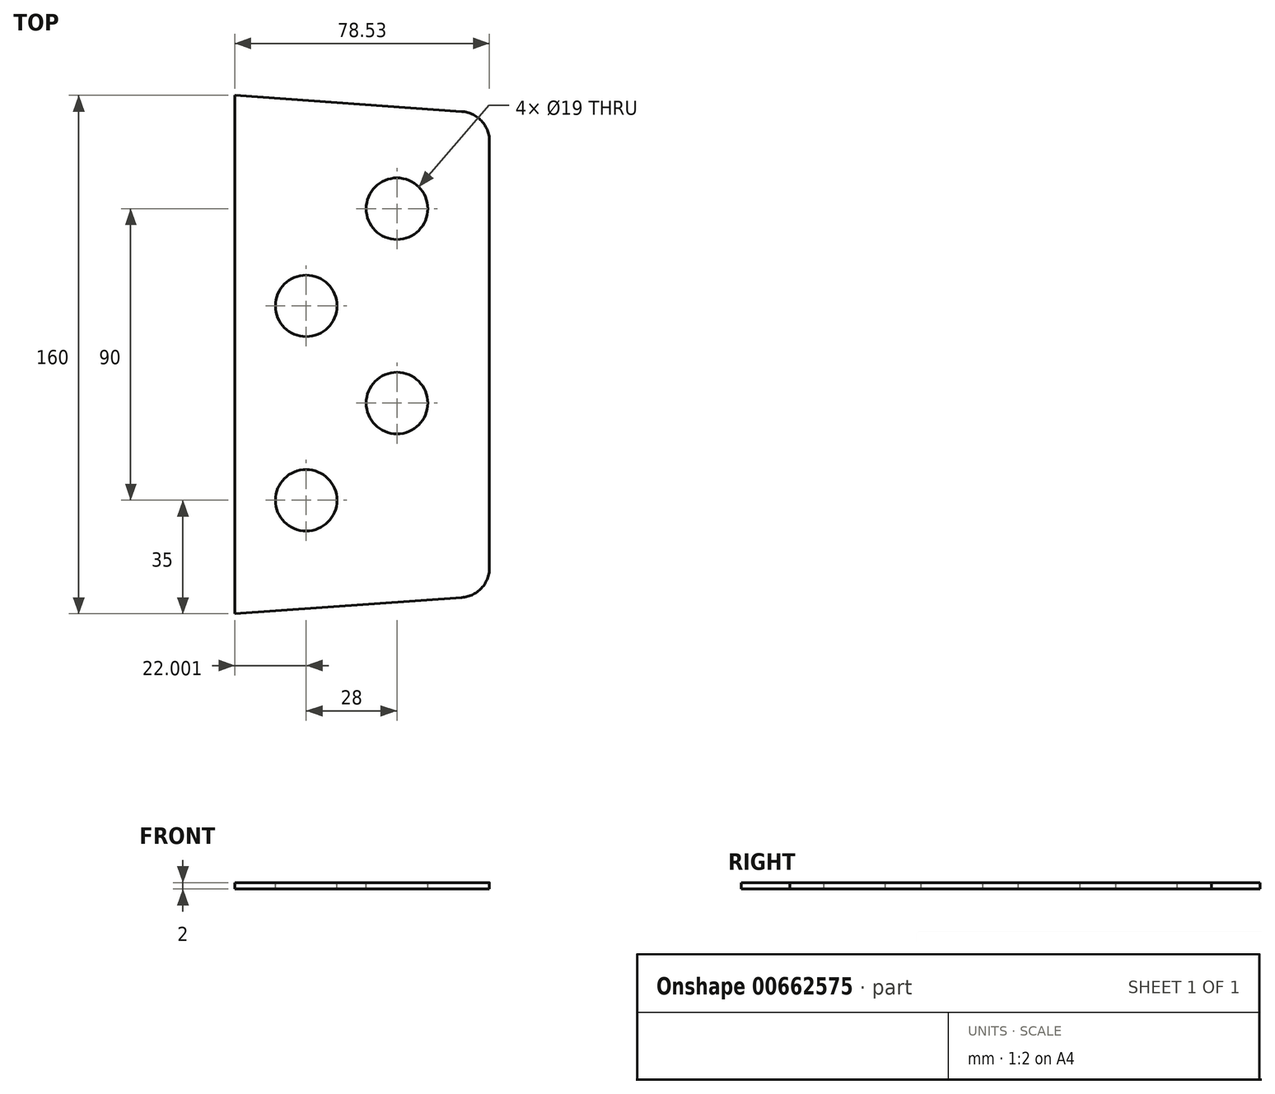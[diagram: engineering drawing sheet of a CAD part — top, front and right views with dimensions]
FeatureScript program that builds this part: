
annotation { "Feature Type Name" : "Feature", "Feature Type Description" : "" }
export const myFeature = defineFeature(function(context is Context, id is Id, definition is map)
    precondition{}
    {
        {
            var Q0;
            Q0=qCreatedBy(makeId("Top.planeOp"),FACE);
            var sketch = newSketch(context, id + "F0", { "sketchPlane" : qUnion([Q0])});
            skLineSegment(sketch, "E0", {"start": v(-42.79, 80) * mm, "end": v(-42.79, -80) * mm});
            skLineSegment(sketch, "E1", {"start": v(-42.79, 80) * mm, "end": v(27.21, 75) * mm});
            skLineSegment(sketch, "E2.MirrorCS", {"start": v(-42.79, -80) * mm, "end": v(27.21, -75) * mm});
            skLineSegment(sketch, "E3", {"start": v(35.7, 65) * mm, "end": v(35.7, -65) * mm});
            skArc(sketch, "E4", {"start": v(27.21, -75) * mm, "mid": v(33.56, -71.78) * mm, "end": v(35.7, -65) * mm});
            skArc(sketch, "E5", {"start": v(27.21, 75) * mm, "mid": v(33.56, 71.78) * mm, "end": v(35.7, 65) * mm});
            skSolve(sketch);
        }
        {
            var Q0;
            Q0=makeQuery(id+"F0.imprint","IMPRINT",FACE,{"disambiguationData":[TD([[makeQuery(id+"F0.imprint","IMPRINT",EDGE,{"derivedFrom":sQuery(id+"F0.wireOp",EDGE,"E0")}),1.0]])]});
            extrude(context, id + "F1", {"entities" : qUnion([Q0]), "depth" : 2 * mm, "offsetDistance" : 25 * mm});
        }
        {
            var Q0;
            Q0=makeQuery(id+"F1.opExtrude","CAP_FACE",FACE,{"disambiguationData":[OSD([sQuery(id+"F0.wireOp",EDGE,"E0"),sQuery(id+"F0.wireOp",EDGE,"E1"),sQuery(id+"F0.wireOp",EDGE,"E2.MirrorCS"),sQuery(id+"F0.wireOp",EDGE,"E3"),sQuery(id+"F0.wireOp",EDGE,"E4"),sQuery(id+"F0.wireOp",EDGE,"E5")])],"isStart":false});
            var sketch = newSketch(context, id + "F2", { "sketchPlane" : qUnion([Q0])});
            skLineSegment(sketch, "E6.0", {"start": v(-42.79, 80) * mm, "end": v(27.21, 75) * mm});
            skLineSegment(sketch, "E7", {"start": v(-20.79, 86.42) * mm, "end": v(-20.79, -83.07) * mm, "construction": true});
            skLineSegment(sketch, "E8", {"start": v(7.21, 84.15) * mm, "end": v(7.21, -82.57) * mm, "construction": true});
            skLineSegment(sketch, "E9", {"start": v(-83, 0) * mm, "end": v(59.47, 0) * mm, "construction": true});
            skLineSegment(sketch, "E10", {"start": v(-82.75, 15) * mm, "end": v(67.55, 15) * mm, "construction": true});
            skLineSegment(sketch, "E11", {"start": v(-78.65, 45) * mm, "end": v(63.97, 45) * mm, "construction": true});
            skCircle(sketch, "E12", {"center": v(-20.79, 15) * mm, "radius": 17.5 * mm, "construction": true});
            skCircle(sketch, "E13", {"center": v(7.21, 45) * mm, "radius": 17.5 * mm, "construction": true});
            skLineSegment(sketch, "E14", {"start": v(-82.94, -15) * mm, "end": v(62.1, -15) * mm, "construction": true});
            skLineSegment(sketch, "E15", {"start": v(-81.74, -45) * mm, "end": v(58.89, -45) * mm, "construction": true});
            skCircle(sketch, "E16", {"center": v(7.21, -15) * mm, "radius": 17.5 * mm, "construction": true});
            skCircle(sketch, "E17", {"center": v(-20.79, -45) * mm, "radius": 17.5 * mm, "construction": true});
            skCircle(sketch, "E18", {"center": v(7.21, 45) * mm, "radius": 9.5 * mm});
            skCircle(sketch, "E19", {"center": v(-20.79, 15) * mm, "radius": 9.5 * mm});
            skCircle(sketch, "E20", {"center": v(7.21, -15) * mm, "radius": 9.5 * mm});
            skCircle(sketch, "E21", {"center": v(-20.79, -45) * mm, "radius": 9.5 * mm});
            skSolve(sketch);
        }
        {
            var Q0;
            Q0=makeQuery(id+"F2.imprint","IMPRINT",FACE,{"disambiguationData":[TD([[makeQuery(id+"F2.imprint","IMPRINT",EDGE,{"derivedFrom":sQuery(id+"F2.wireOp",EDGE,"E18")}),1.0]])]});
            var Q1;
            Q1=makeQuery(id+"F2.imprint","IMPRINT",FACE,{"disambiguationData":[TD([[makeQuery(id+"F2.imprint","IMPRINT",EDGE,{"derivedFrom":sQuery(id+"F2.wireOp",EDGE,"E19")}),1.0]])]});
            var Q2;
            Q2=makeQuery(id+"F2.imprint","IMPRINT",FACE,{"disambiguationData":[TD([[makeQuery(id+"F2.imprint","IMPRINT",EDGE,{"derivedFrom":sQuery(id+"F2.wireOp",EDGE,"E20")}),1.0]])]});
            var Q3;
            Q3=makeQuery(id+"F2.imprint","IMPRINT",FACE,{"disambiguationData":[TD([[makeQuery(id+"F2.imprint","IMPRINT",EDGE,{"derivedFrom":sQuery(id+"F2.wireOp",EDGE,"E21")}),1.0]])]});
            extrude(context, id + "F3", {"entities" : qUnion([Q0, Q1, Q2, Q3]), "operationType" : NewBodyOperationType.REMOVE, "endBound" : BoundingType.UP_TO_NEXT, "oppositeDirection" : true, "depth" : 25 * mm, "offsetDistance" : 25 * mm});
        }
    });
